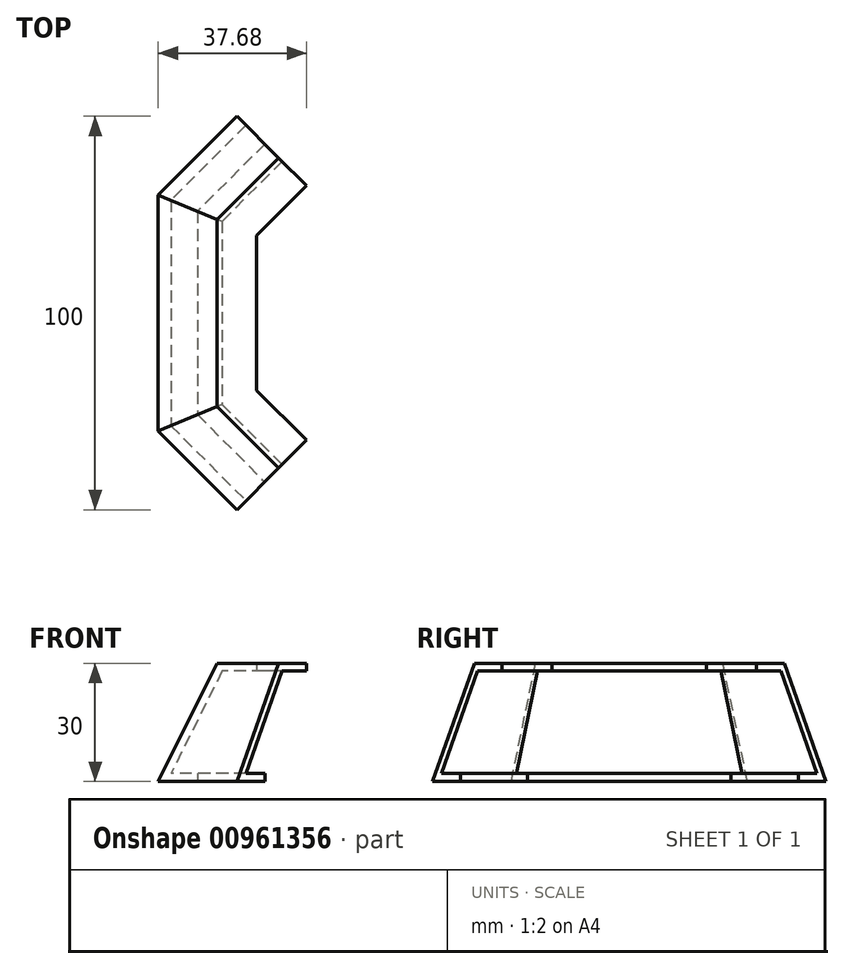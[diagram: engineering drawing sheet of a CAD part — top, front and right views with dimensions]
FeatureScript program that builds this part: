
annotation { "Feature Type Name" : "Feature", "Feature Type Description" : "" }
export const myFeature = defineFeature(function(context is Context, id is Id, definition is map)
    precondition{}
    {
        {
            var Q0;
            Q0=qCreatedBy(makeId("Top.planeOp"),FACE);
            var sketch = newSketch(context, id + "F0", { "sketchPlane" : qUnion([Q0])});
            skLineSegment(sketch, "E0", {"start": v(-20, 30) * mm, "end": v(-20, -30) * mm});
            skLineSegment(sketch, "E1", {"start": v(-20, 30) * mm, "end": v(0, 50) * mm});
            skLineSegment(sketch, "E2", {"start": v(-20, -30) * mm, "end": v(0, -50) * mm});
            skSolve(sketch);
        }
        {
            var Q0;
            Q0=qCreatedBy(makeId("Front.planeOp"),FACE);
            var sketch = newSketch(context, id + "F1", { "sketchPlane" : qUnion([Q0])});
            skLineSegment(sketch, "E3", {"start": v(-10, 0) * mm, "end": v(-20, 0) * mm});
            skLineSegment(sketch, "E4", {"start": v(-20, 0) * mm, "end": v(-5, 30) * mm});
            skLineSegment(sketch, "E5", {"start": v(-5, 30) * mm, "end": v(5, 30) * mm});
            skLineSegment(sketch, "E6", {"start": v(5, 30) * mm, "end": v(5, 28) * mm});
            skLineSegment(sketch, "E7", {"start": v(5, 28) * mm, "end": v(-3.76, 28) * mm});
            skLineSegment(sketch, "E8", {"start": v(-3.76, 28) * mm, "end": v(-16.76, 2) * mm});
            skLineSegment(sketch, "E9", {"start": v(-16.76, 2) * mm, "end": v(-10, 2) * mm});
            skLineSegment(sketch, "E10", {"start": v(-10, 2) * mm, "end": v(-10, 0) * mm});
            skSolve(sketch);
        }
        {
            var Q0;
            Q0=makeQuery(id+"F1.imprint","IMPRINT",FACE,{"disambiguationData":[TD([[makeQuery(id+"F1.imprint","IMPRINT",EDGE,{"derivedFrom":sQuery(id+"F1.wireOp",EDGE,"E3")}),-1.0]])]});
            var Q1;
            Q1=sQuery(id+"F0.wireOp",EDGE,"E0");
            var Q2;
            Q2=sQuery(id+"F0.wireOp",EDGE,"E2");
            var Q3;
            Q3=sQuery(id+"F0.wireOp",EDGE,"E1");
            sweep(context, id + "F2", {"profiles" : qUnion([Q0]), "path" : qUnion([Q1, Q2, Q3])});
        }
    });
